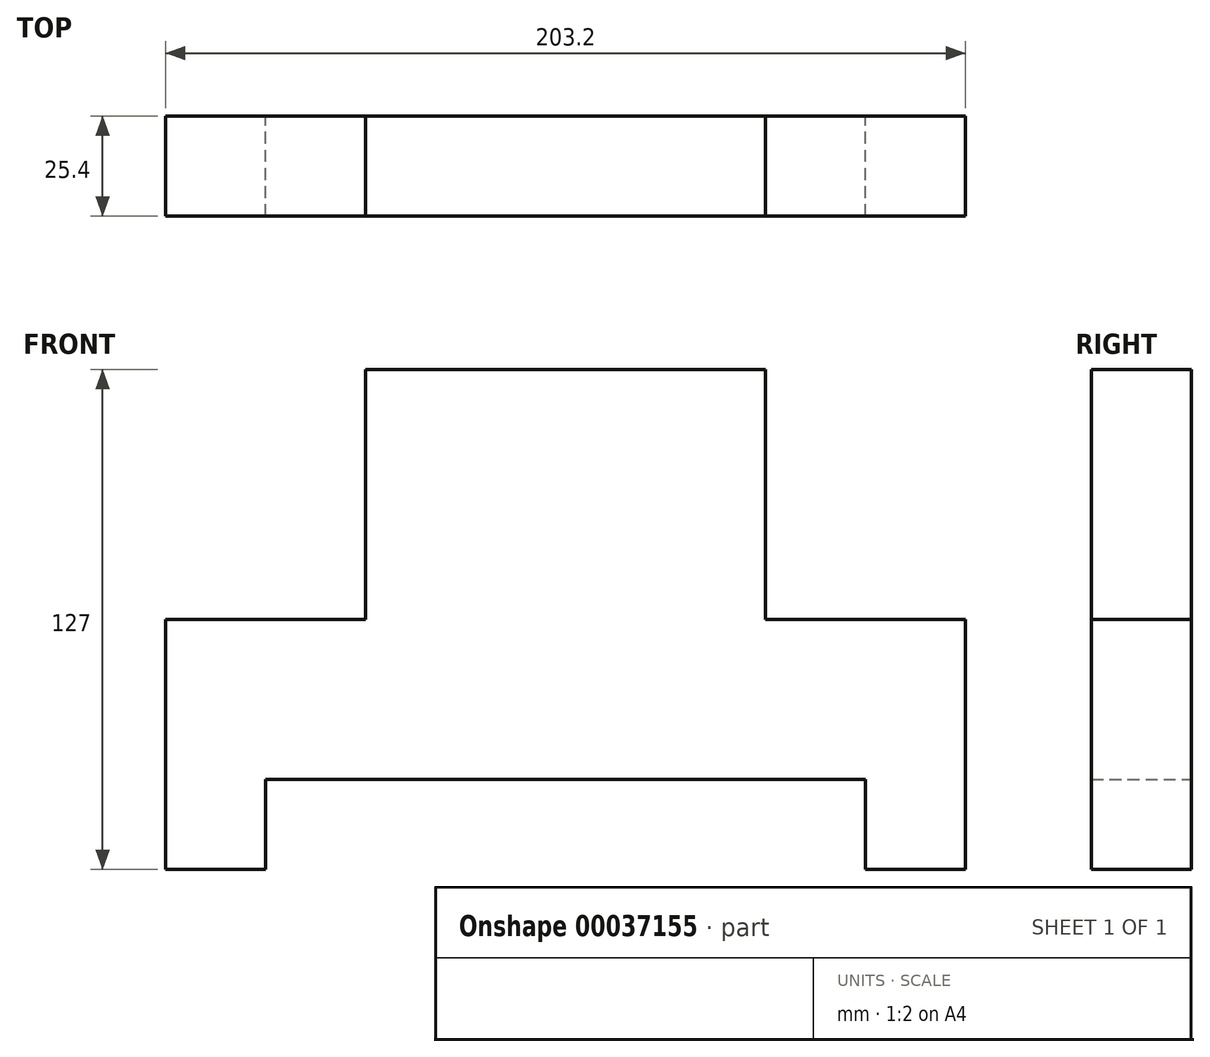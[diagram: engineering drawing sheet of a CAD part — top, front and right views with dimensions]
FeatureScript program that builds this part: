
annotation { "Feature Type Name" : "Feature", "Feature Type Description" : "" }
export const myFeature = defineFeature(function(context is Context, id is Id, definition is map)
    precondition{}
    {
        {
            var Q0;
            Q0=qCreatedBy(makeId("Front.planeOp"),FACE);
            var sketch = newSketch(context, id + "F0", { "sketchPlane" : qUnion([Q0])});
            skLineSegment(sketch, "E0", {"start": v(-93.51, -64.12) * mm, "end": v(-68.11, -64.12) * mm});
            skLineSegment(sketch, "E1", {"start": v(-68.11, -64.12) * mm, "end": v(-68.11, -41.2) * mm});
            skLineSegment(sketch, "E2", {"start": v(-68.11, -41.2) * mm, "end": v(84.29, -41.2) * mm});
            skLineSegment(sketch, "E3", {"start": v(84.29, -41.2) * mm, "end": v(84.29, -64.12) * mm});
            skLineSegment(sketch, "E4", {"start": v(84.29, -64.12) * mm, "end": v(109.69, -64.12) * mm});
            skLineSegment(sketch, "E5", {"start": v(109.69, -64.12) * mm, "end": v(109.69, -0.62) * mm});
            skLineSegment(sketch, "E6", {"start": v(109.69, -0.62) * mm, "end": v(58.89, -0.62) * mm});
            skLineSegment(sketch, "E7", {"start": v(58.89, -0.62) * mm, "end": v(58.89, 62.88) * mm});
            skLineSegment(sketch, "E8", {"start": v(58.89, 62.88) * mm, "end": v(-42.71, 62.88) * mm});
            skLineSegment(sketch, "E9", {"start": v(-42.71, 62.88) * mm, "end": v(-42.71, -0.62) * mm});
            skLineSegment(sketch, "E10", {"start": v(-42.71, -0.62) * mm, "end": v(-93.51, -0.62) * mm});
            skLineSegment(sketch, "E11", {"start": v(-93.51, -0.62) * mm, "end": v(-93.51, -64.12) * mm});
            skSolve(sketch);
        }
        {
            var Q0;
            Q0 = qSketchRegion(id + "F0", true);
            extrude(context, id + "F1", {"entities" : qUnion([Q0]), "depth" : 25.4 * mm});
        }
    });
